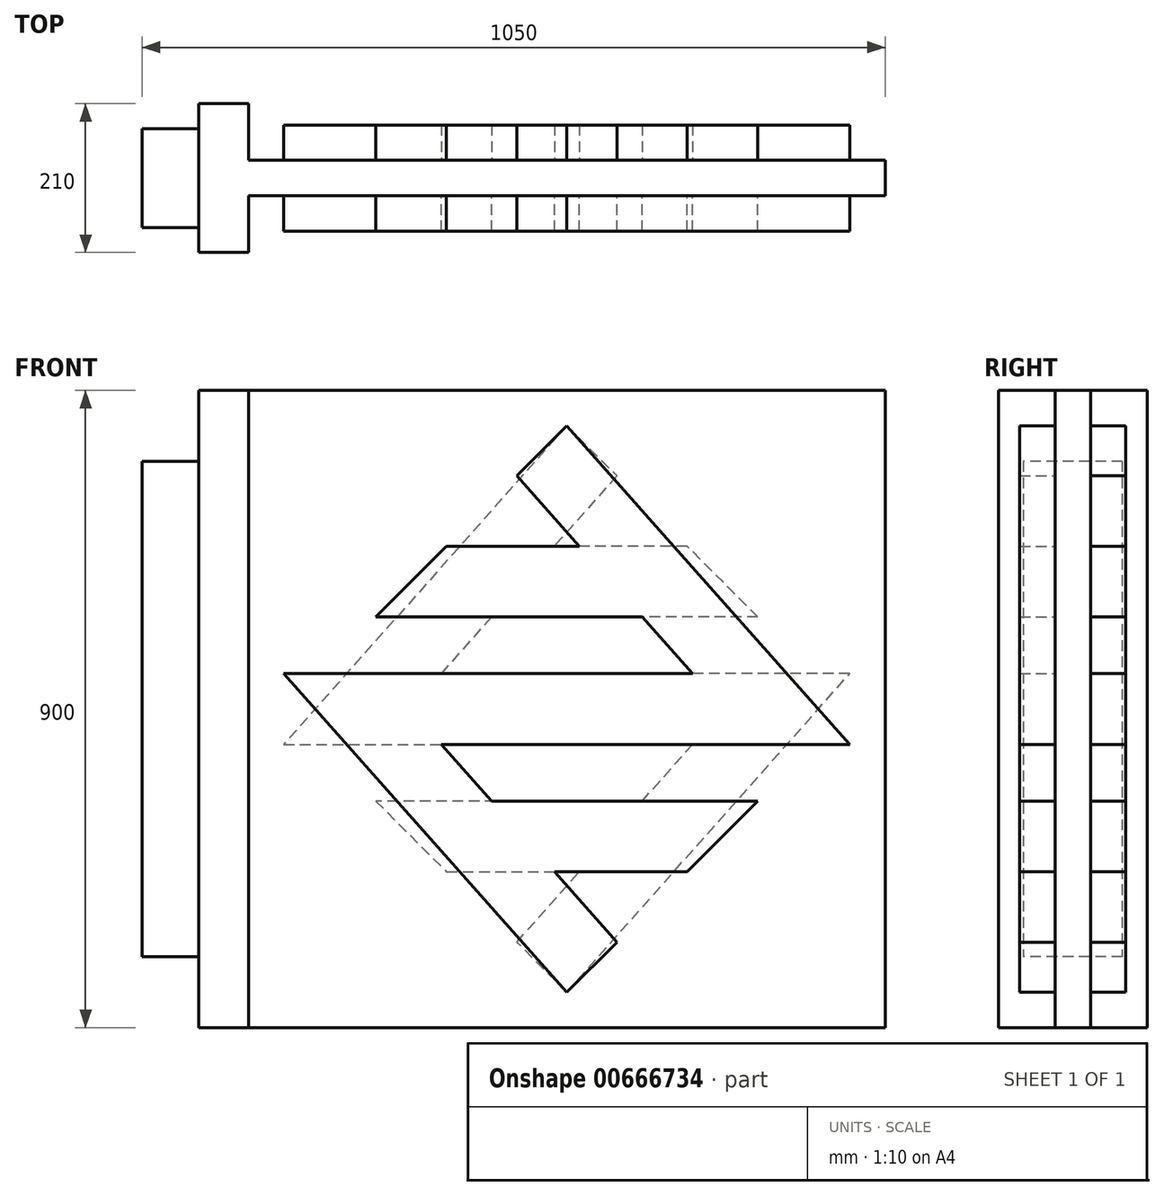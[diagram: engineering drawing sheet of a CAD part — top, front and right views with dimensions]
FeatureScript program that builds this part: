
annotation { "Feature Type Name" : "Feature", "Feature Type Description" : "" }
export const myFeature = defineFeature(function(context is Context, id is Id, definition is map)
    precondition{}
    {
        {
            var Q0;
            Q0=qCreatedBy(makeId("Front.planeOp"),FACE);
            var sketch = newSketch(context, id + "F0", { "sketchPlane" : qUnion([Q0])});
            skLineSegment(sketch, "E0.bottom", {"start": v(-450, 450) * mm, "end": v(450, 450) * mm});
            skLineSegment(sketch, "E0.top", {"start": v(-450, -450) * mm, "end": v(450, -450) * mm});
            skLineSegment(sketch, "E0.left", {"start": v(-450, 450) * mm, "end": v(-450, -450) * mm, "construction": true});
            skLineSegment(sketch, "E0.right", {"start": v(450, 450) * mm, "end": v(450, -450) * mm});
            skPoint(sketch, "E1.firstSnap0", {"position": v(0, -450) * mm});
            skPoint(sketch, "E1.oppositeSnap0", {"position": v(0, -450) * mm});
            skLineSegment(sketch, "E2", {"start": v(-450, 450) * mm, "end": v(-500, 450) * mm});
            skLineSegment(sketch, "E3", {"start": v(-500, 450) * mm, "end": v(-500, -450) * mm});
            skLineSegment(sketch, "E4", {"start": v(-500, -450) * mm, "end": v(-450, -450) * mm});
            skSolve(sketch);
        }
        {
            var Q0;
            Q0=makeQuery(id+"F0.imprint","IMPRINT",FACE,{"disambiguationData":[TD([[makeQuery(id+"F0.imprint","IMPRINT",EDGE,{"derivedFrom":sQuery(id+"F0.wireOp",EDGE,"E0.bottom")}),-1.0]])]});
            extrude(context, id + "F1", {"entities" : qUnion([Q0]), "depth" : 50 * mm, "offsetDistance" : 25 * mm, "symmetric" : true});
        }
        {
            var Q0;
            Q0=makeQuery(id+"F1.opExtrude","CAP_FACE",FACE,{"disambiguationData":[OSD([sQuery(id+"F0.wireOp",EDGE,"E0.bottom"),sQuery(id+"F0.wireOp",EDGE,"E0.top"),sQuery(id+"F0.wireOp",EDGE,"E0.right"),sQuery(id+"F0.wireOp",EDGE,"E2"),sQuery(id+"F0.wireOp",EDGE,"E3"),sQuery(id+"F0.wireOp",EDGE,"E4")])],"isStart":false});
            var sketch = newSketch(context, id + "F2", { "sketchPlane" : qUnion([Q0])});
            skLineSegment(sketch, "E5.bottom", {"start": v(-520, 400) * mm, "end": v(-450, 400) * mm});
            skLineSegment(sketch, "E5.top", {"start": v(-520, -400) * mm, "end": v(-450, -400) * mm});
            skLineSegment(sketch, "E5.left", {"start": v(-520, 400) * mm, "end": v(-520, -400) * mm});
            skLineSegment(sketch, "E5.right", {"start": v(-450, 400) * mm, "end": v(-450, -400) * mm});
            skSolve(sketch);
        }
        {
            var Q0;
            Q0=qSketchRegion(id+"F2",true);
            extrude(context, id + "F3", {"entities" : qUnion([Q0]), "depth" : 80 * mm, "offsetDistance" : 25 * mm});
        }
        {
            var Q0;
            Q0=makeQuery(id+"F3.opExtrude","SWEPT_BODY",BODY,{"disambiguationData":[OSD([sQuery(id+"F2.wireOp",EDGE,"E5.bottom"),sQuery(id+"F2.wireOp",EDGE,"E5.top"),sQuery(id+"F2.wireOp",EDGE,"E5.left"),sQuery(id+"F2.wireOp",EDGE,"E5.right")])]});
            var Q1;
            Q1=qCreatedBy(makeId("Front.planeOp"),FACE);
            mirror(context, id + "F4", {"entities" : qUnion([Q0]), "mirrorPlane" : qUnion([Q1])});
        }
        {
            var Q0;
            Q0=makeQuery(id+"F4.opPattern","COPY",FACE,{"derivedFrom":makeQuery(id+"F3.opExtrude","SWEPT_FACE",FACE,{"disambiguationData":[OSD([sQuery(id+"F2.wireOp",EDGE,"E5.bottom")])]}),"instanceName":"1"});
            var sketch = newSketch(context, id + "F5", { "sketchPlane" : qUnion([Q0])});
            skLineSegment(sketch, "E6.bottom", {"start": v(-520, 25) * mm, "end": v(-500, 25) * mm});
            skLineSegment(sketch, "E6.top", {"start": v(-520, -25) * mm, "end": v(-500, -25) * mm});
            skLineSegment(sketch, "E6.left", {"start": v(-520, 25) * mm, "end": v(-520, -25) * mm});
            skLineSegment(sketch, "E6.right", {"start": v(-500, 25) * mm, "end": v(-500, -25) * mm});
            skSolve(sketch);
        }
        {
            var Q0;
            Q0=qSketchRegion(id+"F5",true);
            var Q1;
            Q1=makeQuery(id+"F4.opPattern","COPY",FACE,{"derivedFrom":makeQuery(id+"F3.opExtrude","SWEPT_FACE",FACE,{"disambiguationData":[OSD([sQuery(id+"F2.wireOp",EDGE,"E5.top")])]}),"instanceName":"1"});
            extrude(context, id + "F6", {"entities" : qUnion([Q0]), "operationType" : NewBodyOperationType.ADD, "endBound" : BoundingType.UP_TO_SURFACE, "oppositeDirection" : true, "depth" : 25 * mm, "endBoundEntityFace" : qUnion([Q1]), "offsetDistance" : 25 * mm});
        }
        {
            var Q0;
            Q0=makeQuery(id+"F1.opExtrude","CAP_FACE",FACE,{"disambiguationData":[OSD([sQuery(id+"F0.wireOp",EDGE,"E0.bottom"),sQuery(id+"F0.wireOp",EDGE,"E0.top"),sQuery(id+"F0.wireOp",EDGE,"E0.right"),sQuery(id+"F0.wireOp",EDGE,"E2"),sQuery(id+"F0.wireOp",EDGE,"E3"),sQuery(id+"F0.wireOp",EDGE,"E4")])],"isStart":false});
            var sketch = newSketch(context, id + "F7", { "sketchPlane" : qUnion([Q0])});
            skLineSegment(sketch, "E7.bottom", {"start": v(-400, 400) * mm, "end": v(400, 400) * mm, "construction": true});
            skLineSegment(sketch, "E7.top", {"start": v(-400, -400) * mm, "end": v(400, -400) * mm, "construction": true});
            skLineSegment(sketch, "E7.left", {"start": v(-400, 400) * mm, "end": v(-400, -400) * mm, "construction": true});
            skLineSegment(sketch, "E7.right", {"start": v(400, 400) * mm, "end": v(400, -400) * mm, "construction": true});
            skLineSegment(sketch, "E8", {"start": v(0, 400) * mm, "end": v(0, -400) * mm, "construction": true});
            skLineSegment(sketch, "E9", {"start": v(-400, 0) * mm, "end": v(400, 0) * mm, "construction": true});
            skLineSegment(sketch, "E10", {"start": v(0, -400) * mm, "end": v(-400, 50) * mm});
            skLineSegment(sketch, "E11", {"start": v(0, 400) * mm, "end": v(400, -50) * mm});
            skLineSegment(sketch, "E12", {"start": v(-400, 0) * mm, "end": v(0, 400) * mm, "construction": true});
            skLineSegment(sketch, "E13", {"start": v(0, 400) * mm, "end": v(-70.71, 329.29) * mm});
            skLineSegment(sketch, "E14", {"start": v(-400, 50) * mm, "end": v(177.55, 50) * mm});
            skLineSegment(sketch, "E15", {"start": v(-70.71, 329.29) * mm, "end": v(17.55, 230) * mm});
            skLineSegment(sketch, "E16", {"start": v(400, -50) * mm, "end": v(-177.55, -50) * mm});
            skLineSegment(sketch, "E17", {"start": v(0, -400) * mm, "end": v(400, 0) * mm, "construction": true});
            skLineSegment(sketch, "E18", {"start": v(0, -400) * mm, "end": v(70.71, -329.29) * mm});
            skLineSegment(sketch, "E19", {"start": v(70.71, -329.29) * mm, "end": v(-17.55, -230) * mm});
            skLineSegment(sketch, "E20", {"start": v(-106.44, -130) * mm, "end": v(270, -130) * mm});
            skLineSegment(sketch, "E21", {"start": v(270, -130) * mm, "end": v(170, -230) * mm});
            skLineSegment(sketch, "E22", {"start": v(170, -230) * mm, "end": v(-17.55, -230) * mm});
            skLineSegment(sketch, "E23.trimOffspring", {"start": v(-106.44, -130) * mm, "end": v(-177.55, -50) * mm});
            skLineSegment(sketch, "E24", {"start": v(-270, 130) * mm, "end": v(106.44, 130) * mm});
            skLineSegment(sketch, "E25", {"start": v(-270, 130) * mm, "end": v(-170, 230) * mm});
            skLineSegment(sketch, "E26", {"start": v(-170, 230) * mm, "end": v(17.55, 230) * mm});
            skLineSegment(sketch, "E27.trimOffspring", {"start": v(106.44, 130) * mm, "end": v(177.55, 50) * mm});
            skSolve(sketch);
        }
        {
            var Q0;
            Q0=qSketchRegion(id+"F7",true);
            extrude(context, id + "F8", {"entities" : qUnion([Q0]), "depth" : 50 * mm, "offsetDistance" : 25 * mm});
        }
        {
            var Q0;
            Q0=makeQuery(id+"F8.opExtrude","SWEPT_BODY",BODY,{"disambiguationData":[OSD([sQuery(id+"F7.wireOp",EDGE,"E10"),sQuery(id+"F7.wireOp",EDGE,"E11"),sQuery(id+"F7.wireOp",EDGE,"E13"),sQuery(id+"F7.wireOp",EDGE,"E14"),sQuery(id+"F7.wireOp",EDGE,"E15"),sQuery(id+"F7.wireOp",EDGE,"E16"),sQuery(id+"F7.wireOp",EDGE,"E18"),sQuery(id+"F7.wireOp",EDGE,"E19"),sQuery(id+"F7.wireOp",EDGE,"E20"),sQuery(id+"F7.wireOp",EDGE,"E21"),sQuery(id+"F7.wireOp",EDGE,"E22"),sQuery(id+"F7.wireOp",EDGE,"E23.trimOffspring"),sQuery(id+"F7.wireOp",EDGE,"E24"),sQuery(id+"F7.wireOp",EDGE,"E25"),sQuery(id+"F7.wireOp",EDGE,"E26"),sQuery(id+"F7.wireOp",EDGE,"E27.trimOffspring")])]});
            var Q1;
            Q1=qCreatedBy(makeId("Front.planeOp"),FACE);
            mirror(context, id + "F9", {"entities" : qUnion([Q0]), "mirrorPlane" : qUnion([Q1])});
        }
        {
            var Q0;
            Q0=makeQuery(id+"F9.opPattern","COPY",BODY,{"derivedFrom":makeQuery(id+"F8.opExtrude","SWEPT_BODY",BODY,{"disambiguationData":[OSD([sQuery(id+"F7.wireOp",EDGE,"E10"),sQuery(id+"F7.wireOp",EDGE,"E11"),sQuery(id+"F7.wireOp",EDGE,"E13"),sQuery(id+"F7.wireOp",EDGE,"E14"),sQuery(id+"F7.wireOp",EDGE,"E15"),sQuery(id+"F7.wireOp",EDGE,"E16"),sQuery(id+"F7.wireOp",EDGE,"E18"),sQuery(id+"F7.wireOp",EDGE,"E19"),sQuery(id+"F7.wireOp",EDGE,"E20"),sQuery(id+"F7.wireOp",EDGE,"E21"),sQuery(id+"F7.wireOp",EDGE,"E22"),sQuery(id+"F7.wireOp",EDGE,"E23.trimOffspring"),sQuery(id+"F7.wireOp",EDGE,"E24"),sQuery(id+"F7.wireOp",EDGE,"E25"),sQuery(id+"F7.wireOp",EDGE,"E26"),sQuery(id+"F7.wireOp",EDGE,"E27.trimOffspring")])]}),"instanceName":"1"});
            var Q1;
            Q1=qCreatedBy(makeId("Right.planeOp"),FACE);
            mirror(context, id + "F10", {"entities" : qUnion([Q0]), "mirrorPlane" : qUnion([Q1])});
        }
        {
            var Q0;
            {var subQ0=makeQuery(id+"F3.opExtrude","SWEPT_FACE",FACE,{"disambiguationData":[OSD([sQuery(id+"F2.wireOp",EDGE,"E5.left")])]});Q0=makeQuery(id+"F6.boolean.opBoolean","MERGE",FACE,{"derivedFrom":[subQ0,makeQuery(id+"F4.opPattern","COPY",FACE,{"derivedFrom":subQ0,"instanceName":"1"}),makeQuery(id+"F6.opExtrude","SWEPT_FACE",FACE,{"disambiguationData":[OSD([sQuery(id+"F5.wireOp",EDGE,"E6.left")])]})]});}
            var sketch = newSketch(context, id + "F11", { "sketchPlane" : qUnion([Q0])});
            skLineSegment(sketch, "E28", {"start": v(0, 400) * mm, "end": v(0, -400) * mm, "construction": true});
            skLineSegment(sketch, "E29.bottom", {"start": v(-70, 350) * mm, "end": v(70, 350) * mm});
            skLineSegment(sketch, "E29.top", {"start": v(-70, -350) * mm, "end": v(70, -350) * mm});
            skLineSegment(sketch, "E29.left", {"start": v(-70, 350) * mm, "end": v(-70, -350) * mm});
            skLineSegment(sketch, "E29.right", {"start": v(70, 350) * mm, "end": v(70, -350) * mm});
            skLineSegment(sketch, "E30", {"start": v(0, 0) * mm, "end": v(-105, 0) * mm, "construction": true});
            skSolve(sketch);
        }
        {
            var Q0;
            Q0=qSketchRegion(id+"F11",true);
            extrude(context, id + "F12", {"entities" : qUnion([Q0]), "depth" : 80 * mm, "offsetDistance" : 25 * mm});
        }
        {
            var Q0;
            {var subQ0=makeQuery(id+"F3.opExtrude","SWEPT_FACE",FACE,{"disambiguationData":[OSD([sQuery(id+"F2.wireOp",EDGE,"E5.bottom")])]});Q0=makeQuery(id+"F6.boolean.opBoolean","MERGE",FACE,{"derivedFrom":[subQ0,makeQuery(id+"F4.opPattern","COPY",FACE,{"derivedFrom":subQ0,"instanceName":"1"}),makeQuery(id+"F6.opExtrude","CAP_FACE",FACE,{"disambiguationData":[OSD([sQuery(id+"F5.wireOp",EDGE,"E6.bottom"),sQuery(id+"F5.wireOp",EDGE,"E6.top"),sQuery(id+"F5.wireOp",EDGE,"E6.left"),sQuery(id+"F5.wireOp",EDGE,"E6.right")])],"isStart":true})]});}
            var Q1;
            Q1=makeQuery(id+"F1.opExtrude","SWEPT_FACE",FACE,{"disambiguationData":[OSD([sQuery(id+"F0.wireOp",EDGE,"E0.bottom"),sQuery(id+"F0.wireOp",EDGE,"E2")])]});
            extrude(context, id + "F13", {"entities" : qUnion([Q0]), "operationType" : NewBodyOperationType.ADD, "endBound" : BoundingType.UP_TO_SURFACE, "depth" : 25 * mm, "endBoundEntityFace" : qUnion([Q1]), "offsetDistance" : 25 * mm});
        }
        {
            var Q0;
            {var subQ0=sQuery(id+"F2.wireOp",EDGE,"E5.top");var subQ1=makeQuery(id+"F3.opExtrude","SWEPT_FACE",FACE,{"disambiguationData":[OSD([subQ0])]});Q0=makeQuery(id+"F6.boolean.opBoolean","MERGE",FACE,{"derivedFrom":[subQ1,makeQuery(id+"F4.opPattern","COPY",FACE,{"derivedFrom":subQ1,"instanceName":"1"}),makeQuery(id+"F6.opExtrude","CAP_FACE",FACE,{"disambiguationData":[OSD([subQ0])],"isStart":false})]});}
            var Q1;
            Q1=makeQuery(id+"F1.opExtrude","SWEPT_FACE",FACE,{"disambiguationData":[OSD([sQuery(id+"F0.wireOp",EDGE,"E0.top"),sQuery(id+"F0.wireOp",EDGE,"E4")])]});
            extrude(context, id + "F14", {"entities" : qUnion([Q0]), "operationType" : NewBodyOperationType.ADD, "endBound" : BoundingType.UP_TO_SURFACE, "depth" : 25 * mm, "endBoundEntityFace" : qUnion([Q1]), "offsetDistance" : 25 * mm});
        }
    });
